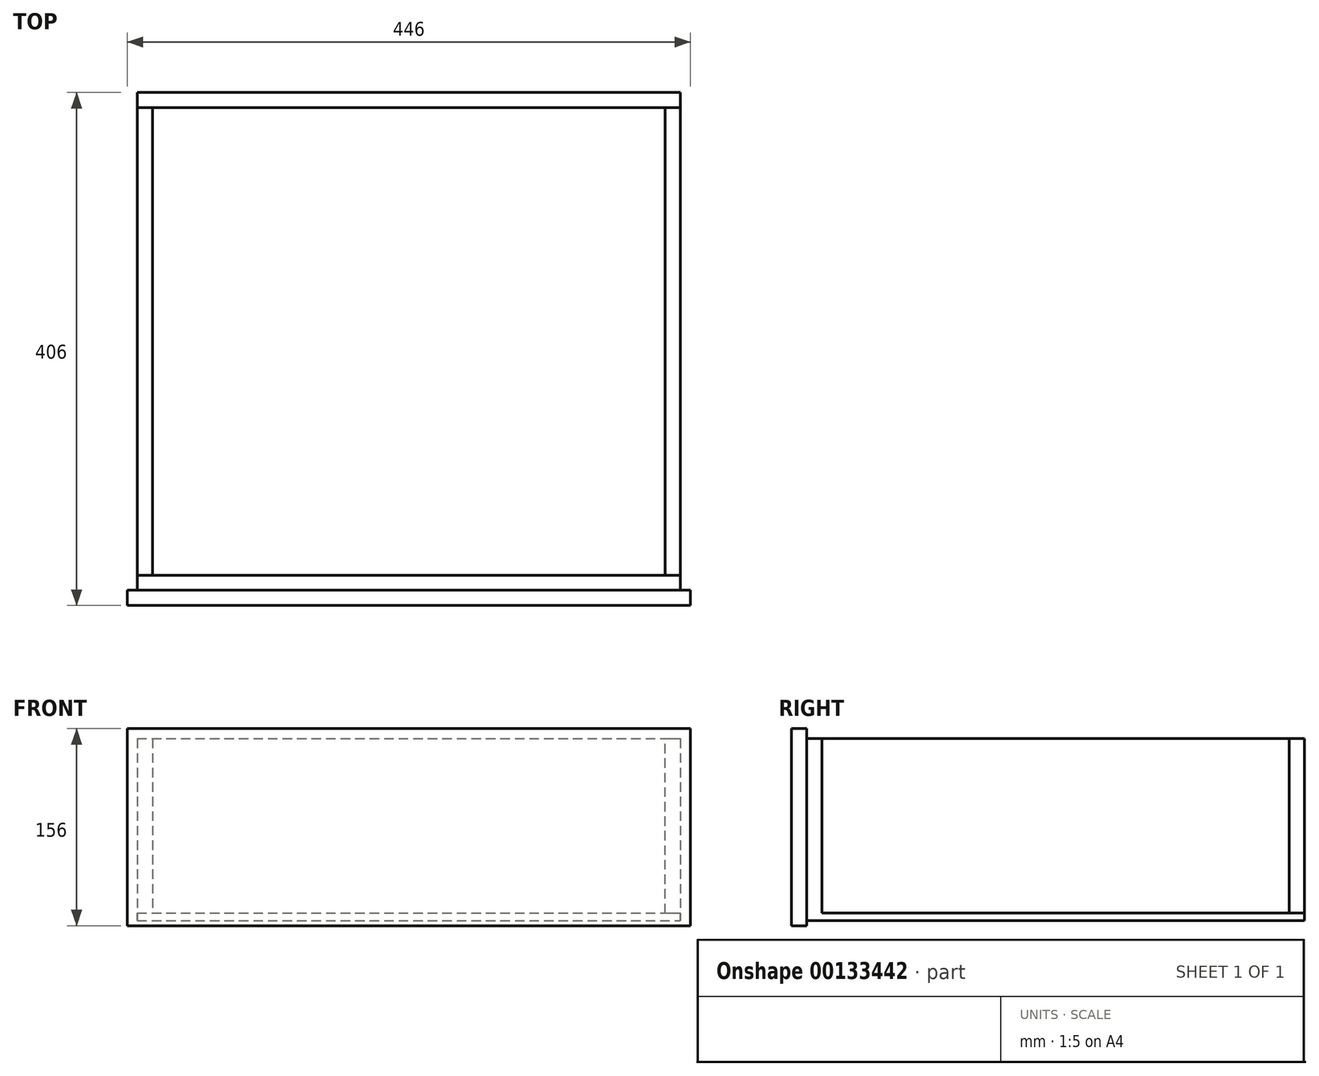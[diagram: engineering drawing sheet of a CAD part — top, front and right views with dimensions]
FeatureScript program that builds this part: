
annotation { "Feature Type Name" : "Feature", "Feature Type Description" : "" }
export const myFeature = defineFeature(function(context is Context, id is Id, definition is map)
    precondition{}
    {
        {
            var Q0;
            Q0=qCreatedBy(makeId("Front.planeOp"),FACE);
            var sketch = newSketch(context, id + "F0", { "sketchPlane" : qUnion([Q0])});
            skLineSegment(sketch, "E0.bottom", {"start": v(-4.7, 121.43) * mm, "end": v(425.3, 121.43) * mm});
            skLineSegment(sketch, "E0.top", {"start": v(-4.7, -16.57) * mm, "end": v(425.3, -16.57) * mm});
            skLineSegment(sketch, "E0.left", {"start": v(-4.7, 121.43) * mm, "end": v(-4.7, -16.57) * mm});
            skLineSegment(sketch, "E0.right", {"start": v(425.3, 121.43) * mm, "end": v(425.3, -16.57) * mm});
            skSolve(sketch);
        }
        {
            var Q0;
            Q0=makeQuery(id+"F0.imprint","IMPRINT",FACE,{"disambiguationData":[TD([[makeQuery(id+"F0.imprint","IMPRINT",EDGE,{"derivedFrom":sQuery(id+"F0.wireOp",EDGE,"E0.bottom")}),-1.0]])]});
            extrude(context, id + "F1", {"entities" : qUnion([Q0]), "depth" : 12 * mm});
        }
        {
            var Q0;
            Q0=makeQuery(id+"F1.opExtrude","CAP_FACE",FACE,{"disambiguationData":[OSD([sQuery(id+"F0.wireOp",EDGE,"E0.bottom"),sQuery(id+"F0.wireOp",EDGE,"E0.top"),sQuery(id+"F0.wireOp",EDGE,"E0.left"),sQuery(id+"F0.wireOp",EDGE,"E0.right")])],"isStart":false});
            var sketch = newSketch(context, id + "F2", { "sketchPlane" : qUnion([Q0])});
            skLineSegment(sketch, "E1.bottom", {"start": v(-4.7, 121.43) * mm, "end": v(7.3, 121.43) * mm});
            skLineSegment(sketch, "E1.top", {"start": v(-4.7, -16.57) * mm, "end": v(7.3, -16.57) * mm});
            skLineSegment(sketch, "E1.left", {"start": v(-4.7, 121.43) * mm, "end": v(-4.7, -16.57) * mm});
            skLineSegment(sketch, "E1.right", {"start": v(7.3, 121.43) * mm, "end": v(7.3, -16.57) * mm});
            skLineSegment(sketch, "E2.bottom", {"start": v(425.3, -16.57) * mm, "end": v(413.3, -16.57) * mm});
            skLineSegment(sketch, "E2.top", {"start": v(425.3, 121.43) * mm, "end": v(413.3, 121.43) * mm});
            skLineSegment(sketch, "E2.left", {"start": v(425.3, -16.57) * mm, "end": v(425.3, 121.43) * mm});
            skLineSegment(sketch, "E2.right", {"start": v(413.3, -16.57) * mm, "end": v(413.3, 121.43) * mm});
            skLineSegment(sketch, "E3", {"start": v(210.3, 121.43) * mm, "end": v(210.3, -16.57) * mm, "construction": true});
            skSolve(sketch);
        }
        {
            var Q0;
            Q0=makeQuery(id+"F2.imprint","IMPRINT",FACE,{"disambiguationData":[TD([[makeQuery(id+"F2.imprint","IMPRINT",EDGE,{"derivedFrom":sQuery(id+"F2.wireOp",EDGE,"E1.bottom")}),-1.0]])]});
            var Q1;
            Q1=makeQuery(id+"F2.imprint","IMPRINT",FACE,{"disambiguationData":[TD([[makeQuery(id+"F2.imprint","IMPRINT",EDGE,{"derivedFrom":sQuery(id+"F2.wireOp",EDGE,"E2.bottom")}),1.0]])]});
            extrude(context, id + "F3", {"entities" : qUnion([Q0, Q1]), "depth" : 370 * mm});
        }
        {
            var Q0;
            Q0=makeQuery(id+"F3.opExtrude","CAP_FACE",FACE,{"disambiguationData":[OSD([sQuery(id+"F2.wireOp",EDGE,"E1.bottom"),sQuery(id+"F2.wireOp",EDGE,"E1.top"),sQuery(id+"F2.wireOp",EDGE,"E1.left"),sQuery(id+"F2.wireOp",EDGE,"E1.right")])],"isStart":false});
            var sketch = newSketch(context, id + "F4", { "sketchPlane" : qUnion([Q0])});
            skPoint(sketch, "E4.0", {"position": v(425.3, 121.43) * mm});
            skPoint(sketch, "E5.0", {"position": v(425.3, -16.57) * mm});
            skLineSegment(sketch, "E6.bottom", {"start": v(-4.7, 121.43) * mm, "end": v(425.3, 121.43) * mm});
            skLineSegment(sketch, "E6.top", {"start": v(-4.7, -16.57) * mm, "end": v(425.3, -16.57) * mm});
            skLineSegment(sketch, "E6.left", {"start": v(-4.7, 121.43) * mm, "end": v(-4.7, -16.57) * mm});
            skLineSegment(sketch, "E6.right", {"start": v(425.3, 121.43) * mm, "end": v(425.3, -16.57) * mm});
            skSolve(sketch);
        }
        {
            var Q0;
            {var subQ2=sQuery(id+"F4.wireOp",EDGE,"E6.right");Q0=makeQuery(id+"F4.imprint","IMPRINT",FACE,{"disambiguationData":[TD([[makeQuery(id+"F4.imprint","IMPRINT",EDGE,{"derivedFrom":subQ2}),-1.0]])]});}
            var Q1;
            {var subQ0=sQuery(id+"F4.wireOp",EDGE,"E6.left");Q1=makeQuery(id+"F4.imprint","IMPRINT",FACE,{"disambiguationData":[TD([[makeQuery(id+"F4.imprint","IMPRINT",EDGE,{"derivedFrom":subQ0}),1.0]])]});}
            extrude(context, id + "F5", {"entities" : qUnion([Q0, Q1]), "depth" : 12 * mm});
        }
        {
            var Q0;
            Q0=makeQuery(id+"F3.opExtrude","SWEPT_FACE",FACE,{"disambiguationData":[OSD([sQuery(id+"F2.wireOp",EDGE,"E1.top")])]});
            var sketch = newSketch(context, id + "F6", { "sketchPlane" : qUnion([Q0])});
            skPoint(sketch, "E7.0", {"position": v(-4.7, 394) * mm});
            skPoint(sketch, "E8.0", {"position": v(425.3, 0) * mm});
            skLineSegment(sketch, "E9.bottom", {"start": v(-4.7, 394) * mm, "end": v(425.3, 394) * mm});
            skLineSegment(sketch, "E9.top", {"start": v(-4.7, 0) * mm, "end": v(425.3, 0) * mm});
            skLineSegment(sketch, "E9.left", {"start": v(-4.7, 394) * mm, "end": v(-4.7, 0) * mm});
            skLineSegment(sketch, "E9.right", {"start": v(425.3, 394) * mm, "end": v(425.3, 0) * mm});
            skSolve(sketch);
        }
        {
            var Q0;
            {var subQ5=sQuery(id+"F6.wireOp",EDGE,"E9.bottom");Q0=makeQuery(id+"F6.imprint","IMPRINT",FACE,{"disambiguationData":[TD([[makeQuery(id+"F6.imprint","IMPRINT",EDGE,{"derivedFrom":subQ5}),-1.0]])]});}
            var Q1;
            {var subQ1=sQuery(id+"F2.wireOp",EDGE,"E1.top");var subQ2=makeQuery(id+"F3.opExtrude","CAP_EDGE",EDGE,{"disambiguationData":[OSD([subQ1])],"isStart":true});Q1=makeQuery(id+"F6.imprint","IMPRINT",FACE,{"disambiguationData":[TD([[makeQuery(id+"F6.imprint","IMPRINT",EDGE,{"derivedFrom":subQ2}),1.0]])]});}
            extrude(context, id + "F7", {"entities" : qUnion([Q0, Q1]), "depth" : 6 * mm});
        }
        {
            var Q0;
            Q0=makeQuery(id+"F5.opExtrude","CAP_FACE",FACE,{"disambiguationData":[OSD([sQuery(id+"F4.wireOp",EDGE,"E6.bottom"),sQuery(id+"F4.wireOp",EDGE,"E6.top"),sQuery(id+"F4.wireOp",EDGE,"E6.left"),sQuery(id+"F4.wireOp",EDGE,"E6.right")])],"isStart":false});
            var sketch = newSketch(context, id + "F8", { "sketchPlane" : qUnion([Q0])});
            skLineSegment(sketch, "E10.bottom", {"start": v(-12.7, 129.43) * mm, "end": v(433.3, 129.43) * mm});
            skLineSegment(sketch, "E10.top", {"start": v(-12.7, -26.57) * mm, "end": v(433.3, -26.57) * mm});
            skLineSegment(sketch, "E10.left", {"start": v(-12.7, 129.43) * mm, "end": v(-12.7, -26.57) * mm});
            skLineSegment(sketch, "E10.right", {"start": v(433.3, 129.43) * mm, "end": v(433.3, -26.57) * mm});
            skLineSegment(sketch, "E11.0", {"start": v(-4.7, 121.43) * mm, "end": v(-4.7, -16.57) * mm, "construction": true});
            skLineSegment(sketch, "E12.0", {"start": v(425.3, 121.43) * mm, "end": v(425.3, -16.57) * mm, "construction": true});
            skLineSegment(sketch, "E13.0", {"start": v(-4.7, 121.43) * mm, "end": v(425.3, 121.43) * mm, "construction": true});
            skLineSegment(sketch, "E14.0", {"start": v(-4.7, -16.57) * mm, "end": v(425.3, -16.57) * mm, "construction": true});
            skPoint(sketch, "E15.0", {"position": v(-4.7, -22.57) * mm});
            skSolve(sketch);
        }
        {
            var Q0;
            Q0=makeQuery(id+"F8.imprint","IMPRINT",FACE,{"disambiguationData":[TD([[makeQuery(id+"F8.imprint","IMPRINT",EDGE,{"derivedFrom":sQuery(id+"F8.wireOp",EDGE,"E10.bottom")}),-1.0]])]});
            var Q1;
            Q1=makeQuery(id+"F8.imprint","IMPRINT",FACE,{"disambiguationData":[TD([[makeQuery(id+"F8.imprint","IMPRINT",EDGE,{"derivedFrom":makeQuery(id+"F5.opExtrude","CAP_EDGE",EDGE,{"disambiguationData":[OSD([sQuery(id+"F4.wireOp",EDGE,"E6.bottom")])],"isStart":false})}),-1.0]])]});
            extrude(context, id + "F9", {"entities" : qUnion([Q0, Q1]), "operationType" : NewBodyOperationType.ADD, "depth" : 12 * mm});
        }
    });
